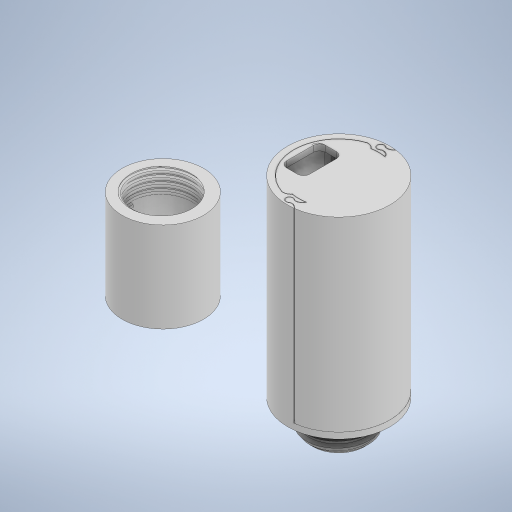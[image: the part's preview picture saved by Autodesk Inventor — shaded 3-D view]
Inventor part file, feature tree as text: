
AUTODESK INVENTOR PART (.ipt)
format: ipt  version: 2024 (Build 280153000, 153)  size: 1,695,744 bytes
history: native  units: in
note: dims shown in document units (in); Inventor stores cm internally (conversion verified against a paired STEP export)
features: sketch x51, extrude x47, plane x9, projected_geometry x9, revolve x5, split x3, move_body x3, other x2, helix x2, boolean_combine x1, chamfer x1, loft x1
ambient origin geometry x8: Origin, YZ Plane, XZ Plane, XY Plane, X Axis, Y Axis, Z Axis, Center Point
bodies: Solid1 (feature_tree), Solid8 (feature_tree), Solid2 (feature_tree), Solid3 (feature_tree), Solid4 (feature_tree), Solid5 (feature_tree), Solid6 (feature_tree), Solid7 (feature_tree)
feature tree (134):
  extrude  "Extrusion1"  Depth=0.1181in
  extrude  "Extrusion2"  Depth=0.8307in
  sketch  "Sketch3"  dims[d7=0.0787in d8=0.0787in d9=0.0in]
  extrude  "Extrusion3"  Depth=0.0787in TaperAngle=0.0deg
  extrude  "Extrusion4"  Depth=0.0787in
  revolve  "Revolution1"  [1 undecoded]
  revolve  "Revolution2"  [1 undecoded]
  plane  "Work Plane2"
  split  "Split1"
  plane  "Work Plane3"
  split  "Split2"
  move_body  "Move Body1"
  move_body  "Move Body2"
  plane  "Work Plane4"
  split  "Split3"
  move_body  "Move Body3"
  boolean_combine  "Combine1"
  sketch  "Sketch12"  dims[d32=0.1181in d33=0.0945in]
  other  "Work Axis1"
  helix  "Coil1"  [1 undecoded]
  sketch  "Sketch13"  dims[d34=0.3937in]
  revolve  "Revolution3"  [1 undecoded]
  revolve  "Revolution4"  [1 undecoded]
  sketch  "Sketch15"  dims[d37=1.4961in]
  other  "Work Axis4"
  chamfer  "Chamfer1"  [1 undecoded]
  helix  "Coil2"  [1 undecoded]
  revolve  "Revolution5"  [1 undecoded]
  extrude  "Extrusion6"  Depth=0.0787in
  plane  "Work Plane5"
  sketch  "Sketch20"  dims[d40=0.315in]
  plane  "Work Plane6"
  extrude  "Extrusion7"  Depth=0.0394in
  extrude  "Extrusion8"  Depth=0.0787in
  extrude  "Extrusion10"  TaperAngle=90.0deg  [1 undecoded]
  extrude  "Extrusion11"  Depth=0.0197in
  extrude  "Extrusion12"  [1 undecoded]
  sketch  "Sketch26"  dims[d51=-1.25in d54=-0.3937in d55=0.0in d56=0.0in d57=-0.3937in d58=0.0in d59=0.0in d60=0.125in]
  plane  "Work Plane7"
  sketch  "Sketch27"  dims[d61=-0.7874in d62=0.0in d63=0.0in d67=0.0394in]
  plane  "Work Plane8"
  loft  "Loft1"
  extrude  "Extrusion13"  Depth=0.0787in TaperAngle=0.0deg
  extrude  "Extrusion14"  Depth=0.0787in
  extrude  "Extrusion15"  Depth=2.3622in TaperAngle=0.0deg
  extrude  "Extrusion16"  Depth=0.0118in
  extrude  "Extrusion17"  Depth=0.0039in
  sketch  "Sketch35"  dims[d98=0.3937in d99=0.0in d100=-0.0315in]
  extrude  "Extrusion18"  Depth=0.0984in
  extrude  "Extrusion19"  Depth=0.0984in
  extrude  "Extrusion20"  Depth=2.3622in TaperAngle=0.0deg
  extrude  "Extrusion21"  Depth=0.0787in TaperAngle=0.0deg
  sketch  "Sketch40"  dims[d137=0.0039in d138=0.0118in]
  extrude  "Extrusion22"  Depth=0.1969in
  extrude  "Extrusion23"  Depth=0.3937in
  extrude  "Extrusion24"  TaperAngle=0.0deg  [1 undecoded]
  extrude  "Extrusion25"  Depth=0.0787in
  sketch  "Sketch41"  dims[d139=0.0177in d140=0.0039in]
  extrude  "Extrusion26"  Depth=5.2963in TaperAngle=0.0deg
  extrude  "Extrusion27"  Depth=0.0197in
  extrude  "Extrusion28"  Depth=2.3622in TaperAngle=0.0deg
  extrude  "Extrusion29"  Depth=0.0039in
  extrude  "Extrusion30"  Depth=0.0039in
  extrude  "Extrusion31"  Depth=2.3622in TaperAngle=0.0deg
  extrude  "Extrusion34"  Depth=0.0039in
  extrude  "Extrusion35"  Depth=2.3622in TaperAngle=0.0deg
  sketch  "Sketch42"  dims[d141=0.0098in d142=0.0984in]
  sketch  "Sketch43"  dims[d143=45.0deg d144=0.0984in]
  extrude  "Extrusion36"  Depth=0.0197in
  extrude  "Extrusion37"  Depth=0.0197in TaperAngle=0.0deg
  extrude  "Extrusion38"  Depth=0.0787in
  extrude  "Extrusion39"  Depth=0.0197in TaperAngle=0.0deg
  extrude  "Extrusion40"  Depth=0.0197in TaperAngle=0.0deg
  extrude  "Extrusion41"  Depth=0.0197in TaperAngle=0.0deg
  sketch  "Sketch48"  dims[d155=0.0in d156=90.0deg d157=0.0in d158=90.0deg]
  extrude  "Extrusion42"  Depth=0.0197in TaperAngle=0.0deg
  extrude  "Extrusion43"  Depth=0.0197in TaperAngle=0.0deg
  extrude  "Extrusion44"  Depth=0.0197in TaperAngle=0.0deg
  extrude  "Extrusion45"  Depth=0.0197in TaperAngle=0.0deg
  extrude  "Extrusion46"  Depth=0.0197in
  extrude  "Extrusion47"  Depth=0.0197in TaperAngle=0.0deg
  sketch  "Sketch54"  dims[d187=0.0039in d189=0.0039in]
  extrude  "Extrusion48"  Depth=0.0197in
  extrude  "Extrusion51"  Depth=0.0197in TaperAngle=0.0deg
  extrude  "Extrusion52"  Depth=0.0197in
  plane  "Work Plane10"
  sketch  "Sketch56"  dims[d194=2.3622in d195=0.0in d197=0.0039in]
  sketch  "Sketch57"  dims[d198=0.0039in d199=2.3622in d200=0.0in]
  extrude  "Extrusion53"  Depth=0.0197in TaperAngle=0.0deg
  sketch  "Sketch1"  dims[d0=0.8307in d1=0.1181in]
  sketch  "Sketch2"  dims[d2=1.1811in d3=0.0in d6=0.8307in]
  sketch  "Sketch4"  dims[d10=0.8268in d11=0.0787in]
  sketch  "Sketch5"  dims[d12=0.3937in d13=0.0in d16=0.0787in d17=0.0in]
  sketch  "Sketch6"  dims[d21=0.0787in d22=0.0787in d25=90.0deg]
  sketch  "Sketch9"  dims[d26=90.0deg d31=0.0787in]
  sketch  "Sketch14"  dims[d35=0.0787in]
  sketch  "Sketch17"  dims[d38=1.4961in]
  sketch  "Sketch18"  dims[d39=0.3996in]
  sketch  "Sketch21"  dims[d41=0.1969in]
  sketch  "Sketch22"  dims[d43=0.0945in]
  sketch  "Sketch23"  dims[d46=0.5728in]
  sketch  "Sketch24"  dims[d47=0.4941in]
  projected_geometry  "Projected Loop1"
  sketch  "Sketch25"  dims[d50=90.0deg]
  projected_geometry  "Projected Loop2"
  sketch  "Sketch29"  dims[d68=0.0787in d69=0.4331in d70=0.3937in d71=0.0in d72=90.0deg d73=90.0deg d74=0.0in d75=0.0in d77=0.0787in]
  sketch  "Sketch30"  dims[d78=90.0deg d79=0.0394in]
  projected_geometry  "Projected Loop3"
  sketch  "Sketch31"  dims[d80=90.0deg d81=0.0787in]
  sketch  "Sketch32"  dims[d82=0.0787in d83=0.0787in d84=45.0deg]
  sketch  "Sketch33"  dims[d85=0.0787in d86=0.4331in d87=0.3937in d88=0.0in d89=90.0deg d90=90.0deg d91=0.0in d92=0.0in d95=90.0deg]
  projected_geometry  "Projected Loop4"
  sketch  "Sketch34"  dims[d96=0.0197in d97=0.0197in]
  sketch  "Sketch36"  dims[d103=0.9in d104=1.5748in d105=0.0in]
  sketch  "Sketch37"  dims[d106=1.3386in d107=0.0787in d108=0.0in]
  sketch  "Sketch38"  dims[d122=0.0787in d133=0.0984in]
  sketch  "Sketch39"  dims[d134=135.0deg d135=2.3622in d136=0.0in]
  sketch  "Sketch44"  dims[d145=135.0deg d146=2.3622in d147=0.0in]
  projected_geometry  "Projected Loop6"
  sketch  "Sketch45"  dims[d148=0.0059in d149=0.0787in d150=0.0in]
  sketch  "Sketch46"  dims[d151=0.1969in d152=0.7874in]
  sketch  "Sketch47"  dims[d153=0.3937in d154=0.8661in]
  sketch  "Sketch49"  dims[d159=0.0in d160=90.0deg d161=0.0787in]
  sketch  "Sketch50"  dims[d162=0.2756in d164=5.2963in d165=0.0in]
  projected_geometry  "Projected Loop7"
  sketch  "Sketch51"  dims[d166=0.0197in d167=0.0039in]
  projected_geometry  "Projected Loop8"
  sketch  "Sketch52"  dims[d169=2.3622in d170=0.0in d171=2.3622in d172=0.0in]
  projected_geometry  "Projected Loop9"
  sketch  "Sketch53"  dims[d173=2.3622in d174=0.0in d186=0.0039in]
  sketch  "Sketch55"  dims[d190=2.3622in d191=0.0in d192=2.3622in d193=0.0in]
  plane  "Work Plane9"
  projected_geometry  "Projected Loop10"
  sketch  "Sketch58"  dims[d201=2.3622in d202=0.0in d211=0.0059in d212=2.3622in d213=0.0in d214=0.0787in d215=2.3622in d216=0.0in d217=2.3622in d218=0.0in d219=2.3622in d220=0.0in d222=2.3622in d223=0.0in d224=2.3622in d225=0.0in d226=2.3622in d227=0.0in d228=2.3622in d229=0.0in d230=0.0059in d231=2.3622in d232=0.0in d233=0.0079in d234=2.3622in d235=0.0in d236=0.0059in d241=2.3622in d242=0.0in d243=2.3622in d244=0.0in d247=0.3232in d248=0.5124in d249=0.0787in d250=0.271in d254=0.0394in d255=0.0394in d256=1.377in d257=0.0in d258=0.0394in d259=0.0394in d260=0.1181in d261=0.0in d262=0.0394in d263=0.0453in d264=0.0in d265=0.5906in d266=0.0in d267=0.5906in d268=0.0in d270=0.0059in d271=0.5906in d272=0.0in d273=0.3035in d274=0.0755in d275=0.3937in d276=0.4719in d277=0.0in d278=0.0787in d279=0.0in d280=0.0787in d281=0.0in d282=0.0787in d283=0.0in d284=0.1713in d285=0.0in d286=0.0787in d287=0.0in d288=0.1575in d289=0.122in d290=0.2441in d291=0.2441in d292=1.3937in d293=0.0in d298=0.063in d299=0.0492in d300=0.0492in d301=1.5748in d303=360.0deg d305=0.6378in d306=0.0in d307=0.4991in d308=0.0in d309=0.0787in d310=0.0in d109=0.0197in d110=0.0344in d168=0.0197in d203=0.0197in d204=0.0344in d311=0.0197in d312=0.0344in d313=0.0197in d314=0.0344in]
note: 11 required parameter values undecoded (feature->parameter linkage not recoverable at this tier; creation-order binding heuristic only, values carry confidence <= 0.55)